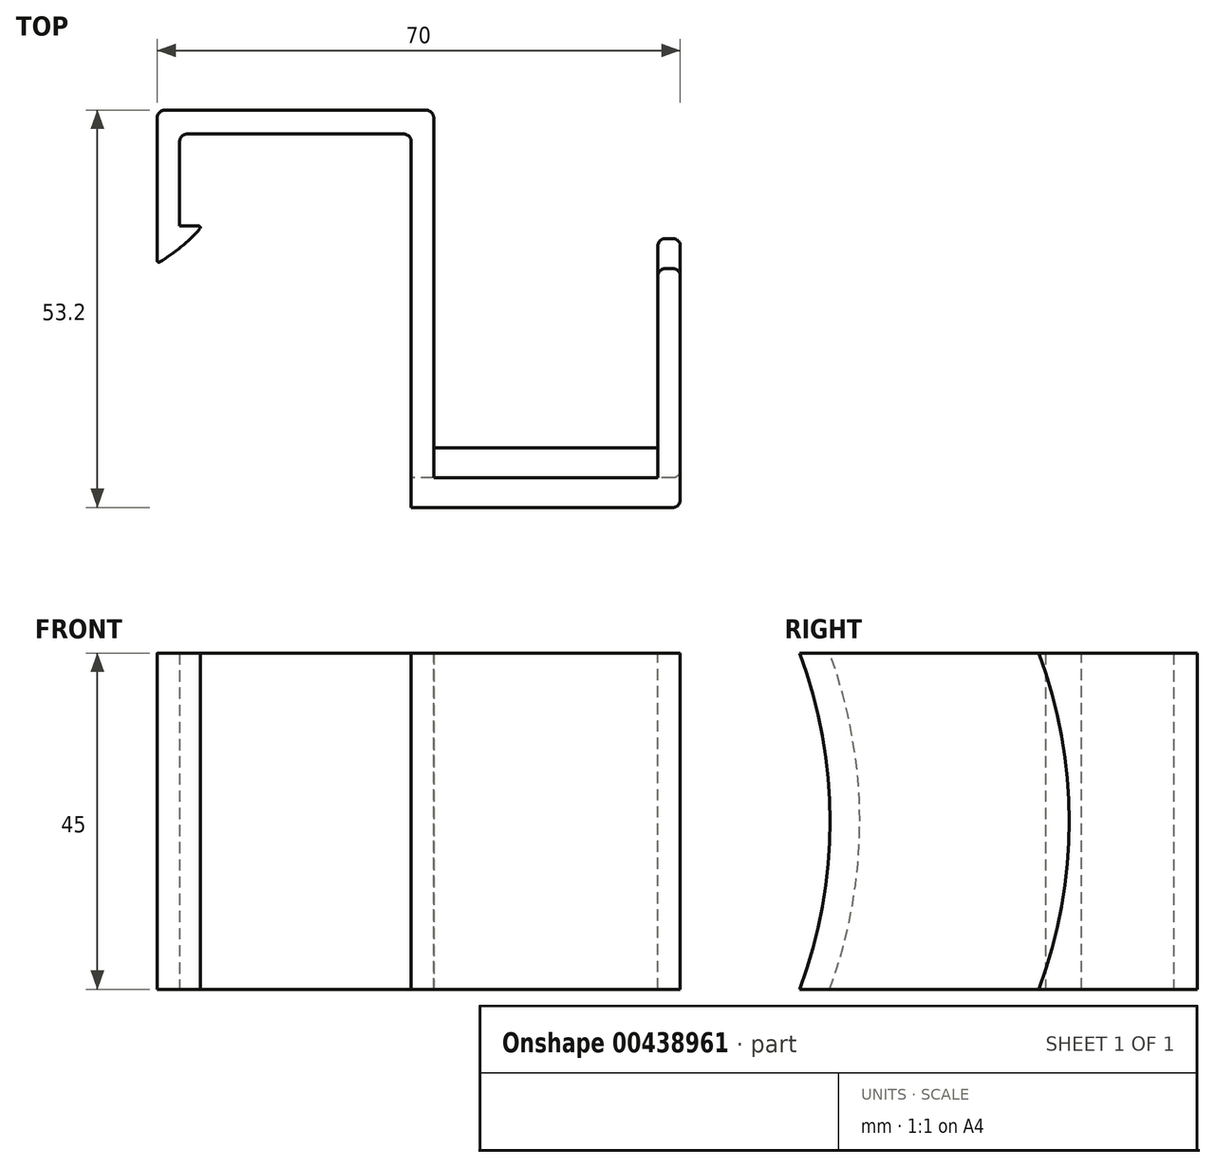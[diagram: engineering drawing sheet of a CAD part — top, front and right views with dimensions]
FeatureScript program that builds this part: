
annotation { "Feature Type Name" : "Feature", "Feature Type Description" : "" }
export const myFeature = defineFeature(function(context is Context, id is Id, definition is map)
    precondition{}
    {
        {
            var Q0;
            Q0=qCreatedBy(makeId("Top.planeOp"),FACE);
            var sketch = newSketch(context, id + "F0", { "sketchPlane" : qUnion([Q0])});
            skLineSegment(sketch, "E0", {"start": v(8.97, 9.85) * mm, "end": v(-22.03, 9.85) * mm});
            skLineSegment(sketch, "E1", {"start": v(-22.03, 9.85) * mm, "end": v(-22.03, -2.45) * mm});
            skLineSegment(sketch, "E2", {"start": v(-22.03, -2.45) * mm, "end": v(-19.03, -2.45) * mm});
            skLineSegment(sketch, "E3", {"start": v(-22.03, -5.42) * mm, "end": v(-22.03, -5.78) * mm, "construction": true});
            skLineSegment(sketch, "E4", {"start": v(-25.03, -7.45) * mm, "end": v(-25.03, 13.05) * mm});
            skLineSegment(sketch, "E5", {"start": v(-25.03, 13.05) * mm, "end": v(11.97, 13.05) * mm});
            skLineSegment(sketch, "E6", {"start": v(8.97, 9.85) * mm, "end": v(8.97, -40.15) * mm});
            skLineSegment(sketch, "E7", {"start": v(8.97, -40.15) * mm, "end": v(11.97, -40.15) * mm});
            skLineSegment(sketch, "E8", {"start": v(11.97, -40.15) * mm, "end": v(11.97, 13.05) * mm});
            skArc(sketch, "E9", {"start": v(-25.03, -7.45) * mm, "mid": v(-21.8, -5.23) * mm, "end": v(-19.03, -2.45) * mm});
            skSolve(sketch);
        }
        {
            var Q0;
            Q0=makeQuery(id+"F0.imprint","IMPRINT",FACE,{"disambiguationData":[TD([[makeQuery(id+"F0.imprint","IMPRINT",EDGE,{"derivedFrom":sQuery(id+"F0.wireOp",EDGE,"E0")}),-1.0]])]});
            extrude(context, id + "F1", {"entities" : qUnion([Q0]), "depth" : 45 * mm});
        }
        {
            var Q0;
            Q0=makeQuery(id+"F1.opExtrude","SWEPT_FACE",FACE,{"disambiguationData":[OSD([sQuery(id+"F0.wireOp",EDGE,"E8")])]});
            var sketch = newSketch(context, id + "F2", { "sketchPlane" : qUnion([Q0])});
            skLineSegment(sketch, "E10", {"start": v(-40.15, 45) * mm, "end": v(-36.15, 45) * mm, "construction": true});
            skLineSegment(sketch, "E11", {"start": v(-40.15, 0) * mm, "end": v(-36.15, 0) * mm, "construction": true});
            skArc(sketch, "E12", {"start": v(-36.15, 0) * mm, "mid": v(-32.13, 22.5) * mm, "end": v(-36.15, 45) * mm});
            skArc(sketch, "E13", {"start": v(-40.15, 0) * mm, "mid": v(-36.13, 22.5) * mm, "end": v(-40.15, 45) * mm});
            skSolve(sketch);
        }
        {
            var Q0;
            {var subQ0=sQuery(id+"F2.wireOp",EDGE,"E12");Q0=makeQuery(id+"F2.imprint","IMPRINT",FACE,{"disambiguationData":[TD([[makeQuery(id+"F2.imprint","IMPRINT",EDGE,{"derivedFrom":subQ0}),1.0]])]});}
            extrude(context, id + "F3", {"entities" : qUnion([Q0]), "operationType" : NewBodyOperationType.ADD, "depth" : 30 * mm});
        }
        {
            var Q0;
            {var subQ2=sQuery(id+"F0.wireOp",EDGE,"E8");var subQ3=sQuery(id+"F0.wireOp",EDGE,"E7");Q0=makeQuery(id+"F3.boolean.opBoolean","SPLIT",FACE,{"disambiguationData":[TD([makeQuery(id+"F1.opExtrude","SWEPT_FACE",FACE,{"disambiguationData":[OSD([subQ3])]})])],"derivedFrom":makeQuery(id+"F1.opExtrude","SWEPT_FACE",FACE,{"disambiguationData":[OSD([subQ2])]})});}
            extrude(context, id + "F4", {"entities" : qUnion([Q0]), "operationType" : NewBodyOperationType.REMOVE, "oppositeDirection" : true, "depth" : 3 * mm});
        }
        {
            var Q0;
            Q0=makeQuery(id+"F3.opExtrude","CAP_FACE",FACE,{"disambiguationData":[OSD([sQuery(id+"F0.wireOp",EDGE,"E8"),sQuery(id+"F2.wireOp",EDGE,"UUv7yDzL-evVW-M6Ao-2L75-DxxvX2bTFWGs"),sQuery(id+"F2.wireOp",EDGE,"oNufuN31-LFaV-OM1X-BK70-01pvX4Go7kuE")])],"isStart":false});
            var sketch = newSketch(context, id + "F5", { "sketchPlane" : qUnion([Q0])});
            skPoint(sketch, "E14.endSnap0", {"position": v(-38.15, 0) * mm});
            skArc(sketch, "E15", {"start": v(-40.15, 0) * mm, "mid": v(-36.13, 22.5) * mm, "end": v(-40.15, 45) * mm});
            skLineSegment(sketch, "E16", {"start": v(-40.15, 45) * mm, "end": v(-8.15, 45) * mm});
            skLineSegment(sketch, "E17", {"start": v(-40.15, 0) * mm, "end": v(-8.15, 0) * mm});
            skArc(sketch, "E18", {"start": v(-8.15, 0) * mm, "mid": v(-4.13, 22.5) * mm, "end": v(-8.15, 45) * mm});
            skSolve(sketch);
        }
        {
            var Q0;
            {var subQ2=sQuery(id+"F5.wireOp",EDGE,"E18");Q0=makeQuery(id+"F5.imprint","IMPRINT",FACE,{"disambiguationData":[TD([[makeQuery(id+"F5.imprint","IMPRINT",EDGE,{"derivedFrom":subQ2}),1.0]])]});}
            var Q1;
            {var subQ0=sQuery(id+"F5.wireOp",EDGE,"E15");Q1=makeQuery(id+"F5.imprint","IMPRINT",FACE,{"disambiguationData":[TD([[makeQuery(id+"F5.imprint","IMPRINT",EDGE,{"derivedFrom":subQ0}),-1.0]])]});}
            extrude(context, id + "F6", {"entities" : qUnion([Q0, Q1]), "operationType" : NewBodyOperationType.ADD, "depth" : 3 * mm});
        }
        {
            var Q0;
            Q0=makeQuery(id+"F1.opExtrude","SWEPT_EDGE",EDGE,{"disambiguationData":[OSD([sQuery(id+"F0.wireOp",EDGE,"E5"),sQuery(id+"F0.wireOp",EDGE,"E8")])]});
            var Q1;
            Q1=makeQuery(id+"F1.opExtrude","SWEPT_EDGE",EDGE,{"disambiguationData":[OSD([sQuery(id+"F0.wireOp",EDGE,"E4"),sQuery(id+"F0.wireOp",EDGE,"E5")])]});
            var Q2;
            Q2=makeQuery(id+"F1.opExtrude","SWEPT_EDGE",EDGE,{"disambiguationData":[OSD([sQuery(id+"F0.wireOp",EDGE,"E0"),sQuery(id+"F0.wireOp",EDGE,"E1")])]});
            var Q3;
            Q3=makeQuery(id+"F1.opExtrude","SWEPT_EDGE",EDGE,{"disambiguationData":[OSD([sQuery(id+"F0.wireOp",EDGE,"E0"),sQuery(id+"F0.wireOp",EDGE,"E6")])]});
            var Q4;
            Q4=makeQuery(id+"F4.boolean.opBoolean","COPY",EDGE,{"derivedFrom":makeQuery(id+"F4.opExtrude","CAP_EDGE",EDGE,{"disambiguationData":[OSD([sQuery(id+"F2.wireOp",EDGE,"E13")])],"isStart":false})});
            var Q5;
            Q5=makeQuery(id+"F6.opExtrude","CAP_EDGE",EDGE,{"disambiguationData":[OSD([sQuery(id+"F5.wireOp",EDGE,"E15")])],"isStart":false});
            var Q6;
            Q6=makeQuery(id+"F6.opExtrude","CAP_EDGE",EDGE,{"disambiguationData":[OSD([sQuery(id+"F5.wireOp",EDGE,"E18")])],"isStart":false});
            var Q7;
            Q7=makeQuery(id+"F6.opExtrude","CAP_EDGE",EDGE,{"disambiguationData":[OSD([sQuery(id+"F5.wireOp",EDGE,"E18")])],"isStart":true});
            var Q8;
            Q8=makeQuery(id+"F3.opExtrude","CAP_EDGE",EDGE,{"disambiguationData":[OSD([sQuery(id+"F2.wireOp",EDGE,"E12")])],"isStart":false});
            var Q9;
            Q9=makeQuery(id+"F3.opExtrude","CAP_EDGE",EDGE,{"disambiguationData":[OSD([sQuery(id+"F2.wireOp",EDGE,"E12")])],"isStart":true});
            fillet(context, id + "F7", {"entities" : qUnion([Q0, Q1, Q2, Q3, Q4, Q5, Q6, Q7, Q8, Q9]), "radius" : 1 * mm, "allowEdgeOverflow" : false});
        }
        {
            var Q0;
            Q0=makeQuery(id+"F1.opExtrude","SWEPT_EDGE",EDGE,{"disambiguationData":[OSD([sQuery(id+"F0.wireOp",EDGE,"E2"),sQuery(id+"F0.wireOp",EDGE,"E9")])]});
            var Q1;
            Q1=makeQuery(id+"F1.opExtrude","SWEPT_EDGE",EDGE,{"disambiguationData":[OSD([sQuery(id+"F0.wireOp",EDGE,"E4"),sQuery(id+"F0.wireOp",EDGE,"E9")])]});
            fillet(context, id + "F8", {"entities" : qUnion([Q0, Q1]), "radius" : 0.2 * mm, "tangentPropagation" : true, "allowEdgeOverflow" : false});
        }
    });
